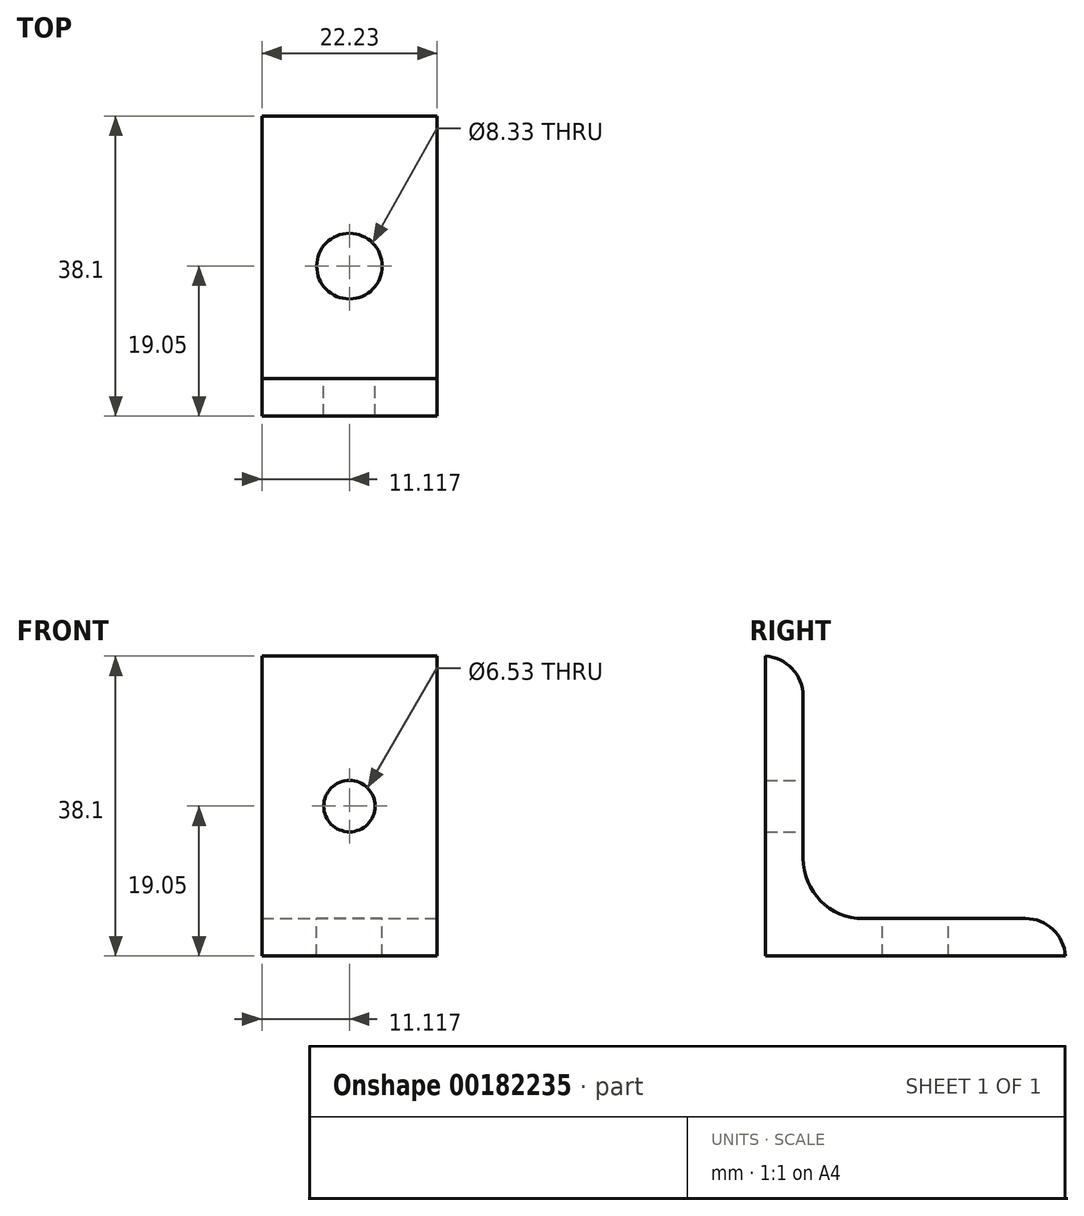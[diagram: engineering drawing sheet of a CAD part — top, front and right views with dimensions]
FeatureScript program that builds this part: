
annotation { "Feature Type Name" : "Feature", "Feature Type Description" : "" }
export const myFeature = defineFeature(function(context is Context, id is Id, definition is map)
    precondition{}
    {
        {
            var Q0;
            Q0=qCreatedBy(makeId("Right.planeOp"),FACE);
            var sketch = newSketch(context, id + "F0", { "sketchPlane" : qUnion([Q0])});
            skLineSegment(sketch, "E0", {"start": v(0, 0) * mm, "end": v(38.1, 0) * mm});
            skLineSegment(sketch, "E1", {"start": v(38.1, 0) * mm, "end": v(38.1, 4.78) * mm});
            skLineSegment(sketch, "E2", {"start": v(38.1, 4.78) * mm, "end": v(4.78, 4.78) * mm});
            skLineSegment(sketch, "E3", {"start": v(4.78, 4.78) * mm, "end": v(4.78, 38.1) * mm});
            skLineSegment(sketch, "E4", {"start": v(4.78, 38.1) * mm, "end": v(0, 38.1) * mm});
            skLineSegment(sketch, "E5", {"start": v(0, 38.1) * mm, "end": v(0, 0) * mm});
            skSolve(sketch);
        }
        {
            var Q0;
            Q0=qSketchRegion(id+"F0",true);
            extrude(context, id + "F1", {"entities" : qUnion([Q0]), "oppositeDirection" : true, "depth" : 22.22 * mm});
        }
        {
            var Q0;
            Q0=makeQuery(id+"F1.opExtrude","SWEPT_EDGE",EDGE,{"disambiguationData":[OSD([sQuery(id+"F0.wireOp",EDGE,"E2"),sQuery(id+"F0.wireOp",EDGE,"E3")])]});
            fillet(context, id + "F2", {"entities" : qUnion([Q0]), "radius" : 7.62 * mm, "tangentPropagation" : true, "allowEdgeOverflow" : false});
        }
        {
            var Q0;
            Q0=makeQuery(id+"F1.opExtrude","SWEPT_EDGE",EDGE,{"disambiguationData":[OSD([sQuery(id+"F0.wireOp",EDGE,"E3"),sQuery(id+"F0.wireOp",EDGE,"E4")])]});
            var Q1;
            Q1=makeQuery(id+"F1.opExtrude","SWEPT_EDGE",EDGE,{"disambiguationData":[OSD([sQuery(id+"F0.wireOp",EDGE,"E1"),sQuery(id+"F0.wireOp",EDGE,"E2")])]});
            fillet(context, id + "F3", {"entities" : qUnion([Q0, Q1]), "radius" : 5.08 * mm, "tangentPropagation" : true, "allowEdgeOverflow" : false});
        }
        {
            var Q0;
            Q0=makeQuery(id+"F1.opExtrude","SWEPT_FACE",FACE,{"disambiguationData":[OSD([sQuery(id+"F0.wireOp",EDGE,"E3")])]});
            var sketch = newSketch(context, id + "F4", { "sketchPlane" : qUnion([Q0])});
            skCircle(sketch, "E6", {"center": v(11.11, 19.05) * mm, "radius": 3.26 * mm});
            skSolve(sketch);
        }
        {
            var Q0;
            Q0=qSketchRegion(id+"F4",true);
            extrude(context, id + "F5", {"entities" : qUnion([Q0]), "operationType" : NewBodyOperationType.REMOVE, "endBound" : BoundingType.THROUGH_ALL, "oppositeDirection" : true, "depth" : 25.4 * mm});
        }
        {
            var Q0;
            Q0=makeQuery(id+"F1.opExtrude","SWEPT_FACE",FACE,{"disambiguationData":[OSD([sQuery(id+"F0.wireOp",EDGE,"E2")])]});
            var sketch = newSketch(context, id + "F6", { "sketchPlane" : qUnion([Q0])});
            skCircle(sketch, "E7", {"center": v(-11.11, 19.05) * mm, "radius": 4.17 * mm});
            skSolve(sketch);
        }
        {
            var Q0;
            Q0=qSketchRegion(id+"F6",true);
            extrude(context, id + "F7", {"entities" : qUnion([Q0]), "operationType" : NewBodyOperationType.REMOVE, "endBound" : BoundingType.THROUGH_ALL, "oppositeDirection" : true, "depth" : 25.4 * mm});
        }
    });
